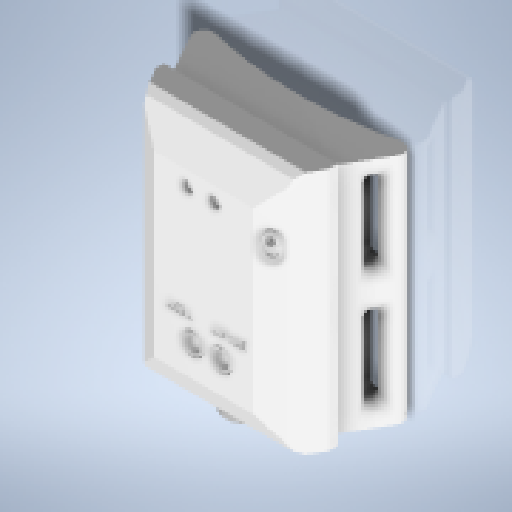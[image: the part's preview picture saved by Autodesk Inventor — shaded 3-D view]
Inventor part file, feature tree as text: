
AUTODESK INVENTOR PART (.ipt)
format: ipt  version: 2024.3 (Build 283343000, 343)  size: 3,822,592 bytes
history: native  units: mm
features: extrude x46, projected_geometry x44, sketch x42, reference x16, fillet x15, other x11, plane x7, chamfer x6, thicken_offset x4, mirror x3, split x3, boolean_combine x2, shell x1
ambient origin geometry x8: Origin, YZ Plane, XZ Plane, XY Plane, X Axis, Y Axis, Z Axis, Center Point
bodies: Solid1 (feature_tree), Solid4 (feature_tree), Solid5 (feature_tree), Solid8 (feature_tree), Solid9 (feature_tree), Solid11 (feature_tree), Solid12 (feature_tree), Solid2 (feature_tree), Solid3 (feature_tree)
feature tree (200):
  extrude  "Extrusion1"  Depth=55.0mm
  extrude  "Extrusion2"  TaperAngle=0.0deg  [1 undecoded]
  extrude  "Extrusion3"  TaperAngle=0.0deg  [1 undecoded]
  fillet  "Fillet1"  Radius=4.0mm
  plane  "Work Plane1"
  extrude  "Extrusion4"  Depth=2.0mm TaperAngle=0.0deg
  fillet  "Fillet2"  Radius=2.0mm
  fillet  "Fillet3"  Radius=5.0mm
  fillet  "Fillet4"  Radius=2.0mm
  mirror  "Mirror1"
  split  "Split1"
  mirror  "Mirror2"
  extrude  "Extrusion5"  Depth=3.0mm
  shell  "Shell1"  Thickness=2.0mm
  plane  "Work Plane2"
  extrude  "Extrusion6"  Depth=2.0mm
  chamfer  "Chamfer1"  Distance=30.0mm
  plane  "Work Plane3"
  extrude  "Extrusion7"  TaperAngle=0.0deg  [1 undecoded]
  extrude  "Extrusion8"  Depth=0.5mm TaperAngle=45.0deg
  split  "Split2"
  extrude  "Extrusion9"  Depth=1.0mm TaperAngle=0.0deg
  extrude  "Extrusion10"  TaperAngle=45.0deg  [1 undecoded]
  mirror  "Mirror3"
  plane  "Work Plane4"
  split  "Split3"
  extrude  "Extrusion11"  Depth=3.0mm TaperAngle=0.0deg
  fillet  "Fillet5"  Radius=2.0mm
  fillet  "Fillet6"  Radius=3.0mm
  extrude  "Extrusion12"  Depth=4.0mm
  extrude  "Extrusion13"  Depth=1.0mm
  thicken_offset  "Thicken1"
  thicken_offset  "Thicken2"
  extrude  "Extrusion14"  Depth=1.0mm
  boolean_combine  "Combine1"
  boolean_combine  "Combine2"
  extrude  "Extrusion15"  Depth=0.5mm
  fillet  "Fillet7"  Radius=0.5mm
  extrude  "Extrusion16"  Depth=2.0mm
  extrude  "Extrusion17"  Depth=1.0mm
  fillet  "Fillet8"  Radius=15.0mm
  sketch  "Sketch18"  dims[d62=2.4mm d63=2.0mm]
  extrude  "Extrusion18"  Depth=2.0mm
  extrude  "Extrusion19"  Depth=2.0mm
  fillet  "Fillet9"  Radius=4.0mm
  extrude  "Extrusion20"  Depth=1.0mm
  thicken_offset  "Thicken3"
  thicken_offset  "Thicken4"
  plane  "Work Plane5"
  extrude  "Extrusion21"  Depth=4.0mm TaperAngle=0.0deg
  chamfer  "Chamfer2"  Distance=10.0mm
  chamfer  "Chamfer3"  Distance=4.0mm
  extrude  "Extrusion22"  Depth=4.0mm TaperAngle=0.0deg
  fillet  "Fillet10"  Radius=10.0mm
  extrude  "Extrusion28"  Depth=0.3mm
  sketch  "Sketch28"  dims[d76=0.7mm]
  extrude  "Extrusion29"  Depth=0.3mm
  extrude  "Extrusion30"  Depth=8.0mm
  extrude  "Extrusion31"  Depth=0.5mm
  extrude  "Extrusion32"  Depth=0.5mm
  fillet  "Fillet11"  Radius=0.5mm
  fillet  "Fillet12"  Radius=0.5mm
  extrude  "Extrusion33"  Depth=2.0mm
  extrude  "Extrusion34"  Depth=2.0mm
  plane  "Work Plane7"
  extrude  "Extrusion35"  Depth=2.0mm TaperAngle=0.0deg
  extrude  "Extrusion36"  Depth=2.0mm
  extrude  "Extrusion37"  Depth=1.0mm
  extrude  "Extrusion38"  Depth=1.0mm
  extrude  "Extrusion39"  Depth=1.0mm
  extrude  "Extrusion40"  Depth=1.0mm
  chamfer  "Chamfer4"  Distance=0.3mm
  chamfer  "Chamfer5"  Distance=4.0mm
  fillet  "Fillet13"  Radius=1.5mm
  sketch  "Sketch38"  dims[d97=1.5mm d98=0.3mm]
  extrude  "Extrusion41"  Depth=4.0mm
  extrude  "Extrusion42"  Depth=2.0mm TaperAngle=0.0deg
  sketch  "Sketch39"  dims[d99=5.0mm d100=0.3mm]
  extrude  "Extrusion43"  Depth=1.0mm TaperAngle=30.0deg
  chamfer  "Chamfer6"  Distance=14.2mm Angle=30.0deg
  extrude  "Extrusion44"  Depth=1.0mm
  plane  "Work Plane8"
  extrude  "Extrusion45"  Depth=3.0mm TaperAngle=0.0deg
  fillet  "Fillet14"  Radius=2.0mm
  extrude  "Extrusion46"  Depth=1.0mm
  extrude  "Extrusion47"  Depth=1.0mm
  extrude  "Extrusion48"  TaperAngle=150.0deg  [1 undecoded]
  extrude  "Extrusion49"  Depth=1.0mm
  extrude  "Extrusion50"  Depth=1.0mm
  extrude  "Extrusion51"  Depth=1.0mm
  fillet  "Fillet15"  Radius=2.0mm
  sketch  "Sketch1"  dims[d0=30.0mm d1=30.0deg d2=55.0mm]
  sketch  "Sketch2"  dims[d3=90.0mm d4=0.0mm d5=0.0mm]
  sketch  "Sketch3"  dims[d6=150.0mm d7=0.0mm d8=0.0mm d9=4.0mm]
  sketch  "Sketch4"  dims[d10=5.0mm d11=30.0mm d12=0.0mm d13=2.0mm d14=5.0mm d15=2.0mm]
  sketch  "Sketch5"  dims[d16=1.5mm d17=3.0mm d18=2.0mm]
  sketch  "Sketch6"  dims[d19=2.0mm d20=30.0mm d22=1.22173mm d24=30.0mm d26=1.22173mm]
  reference  "Reference1"
  sketch  "Sketch7"  dims[d28=0.0mm d29=0.0mm d30=0.0mm d31=0.0mm]
  projected_geometry  "Projected Loop1"
  reference  "Reference2"
  sketch  "Sketch8"  dims[d32=0.2mm d33=0.5mm d34=1.5mm d35=45.0deg]
  projected_geometry  "Projected Loop2"
  sketch  "Sketch9"  dims[d36=2.0mm d37=1.0mm d38=0.0mm]
  projected_geometry  "Projected Loop3"
  sketch  "Sketch10"  dims[d39=1.0mm d40=0.0mm d41=45.0deg]
  projected_geometry  "Projected Loop4"
  sketch  "Sketch11"  dims[d42=20.361989mm d43=15.0mm d44=0.0mm d45=2.0mm d46=3.0mm]
  projected_geometry  "Projected Loop5"
  sketch  "Sketch12"  dims[d47=3.0mm d48=4.0mm]
  projected_geometry  "Projected Loop6"
  projected_geometry  "Projected Loop7"
  sketch  "Sketch13"  dims[d49=4.0mm d50=1.0mm]
  sketch  "Sketch14"  dims[d51=1.0mm d52=1.0mm]
  projected_geometry  "Projected Loop8"
  projected_geometry  "Projected Loop9"
  projected_geometry  "Projected Loop10"
  sketch  "Sketch15"  dims[d53=60.0deg d54=0.5mm d55=0.5mm]
  reference  "Reference3"
  sketch  "Sketch16"  dims[d56=1.8mm d57=2.0mm]
  projected_geometry  "Projected Loop11"
  reference  "Reference4"
  sketch  "Sketch17"  dims[d58=1.2mm d59=1.0mm d60=15.0mm d61=0.0mm]
  projected_geometry  "Projected Loop12"
  projected_geometry  "Projected Loop13"
  sketch  "Sketch19"  dims[d64=5.0mm d65=2.0mm d66=4.0mm d67=0.0mm]
  projected_geometry  "Projected Loop14"
  projected_geometry  "Projected Loop15"
  sketch  "Sketch20"  dims[d68=1.0mm d69=6.1mm]
  reference  "Reference5"
  reference  "Reference6"
  sketch  "Sketch21"  dims[d70=1.5mm d71=4.0mm d72=0.0mm d73=10.0mm d74=0.0mm]
  projected_geometry  "Projected Loop16"
  sketch  "Sketch27"  dims[d75=0.7mm]
  reference  "Reference8"
  reference  "Reference9"
  sketch  "Sketch29"  dims[d77=0.7mm]
  reference  "Reference10"
  reference  "Reference11"
  sketch  "Sketch30"  dims[d78=0.7mm]
  reference  "Reference12"
  reference  "Reference13"
  reference  "Reference14"
  projected_geometry  "Projected Loop25"
  projected_geometry  "Projected Loop26"
  sketch  "Sketch31"  dims[d79=0.25mm]
  projected_geometry  "Projected Loop27"
  sketch  "Sketch32"  dims[d80=0.25mm]
  reference  "Reference15"
  sketch  "Sketch33"  dims[d84=1.5mm]
  projected_geometry  "Projected Loop28"
  sketch  "Sketch34"  dims[d85=1.5mm]
  projected_geometry  "Projected Loop29"
  sketch  "Sketch35"  dims[d86=1.5mm]
  projected_geometry  "Projected Loop30"
  sketch  "Sketch36"  dims[d87=1.5mm d88=4.0mm d89=0.0mm]
  sketch  "Sketch37"  dims[d90=0.25mm d91=4.0mm d92=0.0mm d95=10.0mm d96=0.0mm]
  projected_geometry  "Projected Loop31"
  projected_geometry  "Projected Loop32"
  projected_geometry  "Projected Loop33"
  projected_geometry  "Projected Loop34"
  projected_geometry  "Projected Loop35"
  sketch  "Sketch40"  dims[d101=1.5mm d102=8.0mm]
  reference  "Reference16"
  reference  "Reference17"
  sketch  "Sketch41"  dims[d103=1.2mm d104=0.5mm]
  sketch  "Sketch42"  dims[d105=0.5mm d106=0.5mm d107=0.5mm d108=0.5mm d109=0.0mm]
  projected_geometry  "Projected Loop36"
  sketch  "Sketch43"  dims[d110=0.5mm d111=2.0mm]
  sketch  "Sketch44"  dims[d112=0.3mm d113=2.0mm]
  projected_geometry  "Projected Loop37"
  sketch  "Sketch45"  dims[d114=2.0mm d115=0.0mm d116=2.0mm d117=0.0mm]
  projected_geometry  "Projected Loop38"
  projected_geometry  "Projected Loop39"
  projected_geometry  "Projected Loop40"
  projected_geometry  "Projected Loop41"
  projected_geometry  "Projected Loop42"
  projected_geometry  "Projected Loop43"
  projected_geometry  "Projected Loop44"
  sketch  "Sketch46"  dims[d118=1.0mm d119=2.0mm]
  sketch  "Sketch47"  dims[d120=10.0mm d121=0.0mm d122=0.2mm d123=0.2mm d124=0.2mm d125=0.2mm d126=0.3mm d127=4.0mm d128=1.5mm d129=4.0mm d130=2.0mm d131=0.0mm d132=14.2mm d133=13.25mm d134=30.0deg d135=14.2mm d136=13.25mm d137=30.0deg d138=1.5mm d139=3.0mm d140=0.0mm d141=2.0mm d159=0.5mm d160=0.3mm d163=150.0deg d164=1.5mm d166=5.0mm d167=5.0mm d168=2.0mm d169=106.0mm d170=0.0mm d171=0.3mm d175=60.0deg d176=2.0mm d177=2.7mm d178=120.0deg d179=0.0mm d180=0.0mm d181=10.0mm d182=0.0mm d183=10.0mm d184=0.0mm d185=5.0mm d186=0.3mm d187=0.3mm d190=2.0mm d191=0.3mm d192=0.3mm d193=10.0mm d194=3.490659mm d195=1.0mm d196=0.5mm d197=2.0mm d198=2.0mm d199=2.0mm d200=2.0mm d201=2.0mm d202=2.0mm d203=2.0mm d204=2.0mm d205=2.0mm d206=4.0mm d207=0.0mm d208=0.0mm d209=2.0mm d210=1.0mm d211=-7.853982mm d212=-8.5mm d213=0.3mm d215=1.5mm d216=3.2mm d217=0.0mm d218=1.5mm d219=0.0mm d220=0.3mm d221=0.5mm d222=0.0mm d223=1.0mm d224=-5.235988mm d225=4.060254mm d226=1.0mm d227=0.0mm d228=0.5mm d229=1.0mm d230=0.0mm d231=4.13mm d232=1.36mm d233=30.0deg d234=4.1mm d235=2.94mm d236=30.0deg d237=3.0mm d238=2.0mm d239=3.2mm d240=5.5mm d241=-0.349066mm d242=1.5mm d243=0.0mm d244=0.3mm d245=0.3mm d247=60.0deg d248=0.5mm d249=0.5mm d250=6.0mm d251=0.0mm d252=2.0mm d253=6.0mm d254=30.0deg d255=0.4mm d256=0.4mm d257=0.0mm d258=0.0mm d259=60.0deg d260=60.0deg d261=4.0mm d262=1.5mm d263=1.5mm d264=1.5mm d265=0.0mm d266=1.0mm d267=1.0mm d268=1.0mm d269=1.5mm d270=-5.235988mm d271=0.4mm d272=0.0mm d273=6.0mm d274=0.0mm d275=0.3mm d276=0.3mm d277=5.0mm d278=0.3mm d279=0.3mm d280=5.0mm d281=2.0mm d282=0.3mm d283=30.0mm d284=2.0mm d285=3.0mm d286=0.0mm d287=3.0mm d288=0.0mm d289=5.0mm d290=1.0mm d291=4.0mm d292=2.0mm d293=0.0mm d294=1.0mm]
  projected_geometry  "Projected Loop45"
  projected_geometry  "Project Cut Edges1"
  projected_geometry  "Project Cut Edges2"
  projected_geometry  "Project Cut Edges3"
  other  "<userpath> TUF\Documents\Inventor\ParkinsonDetection\Prototy-1.iam"
  other  "Prototy-1.iam"
  other  "Pin:1"
  projected_geometry  "Project Cut Edges4"
  other  "Buzzer:1"
  projected_geometry  "Project Cut Edges5"
  other  "PCB-V1:1"
  projected_geometry  "Project Cut Edges7"
  other  "3296W:2"
  other  "Holder-PCB:1"
  other  "3296W:1"
  other  "Switch:1"
  other  "TACTILE SWITCH:1"
  other  "TACTILE SWITCH:2"
  projected_geometry  "Project Cut Edges8"
note: 5 required parameter values undecoded (feature->parameter linkage not recoverable at this tier; creation-order binding heuristic only, values carry confidence <= 0.55)
